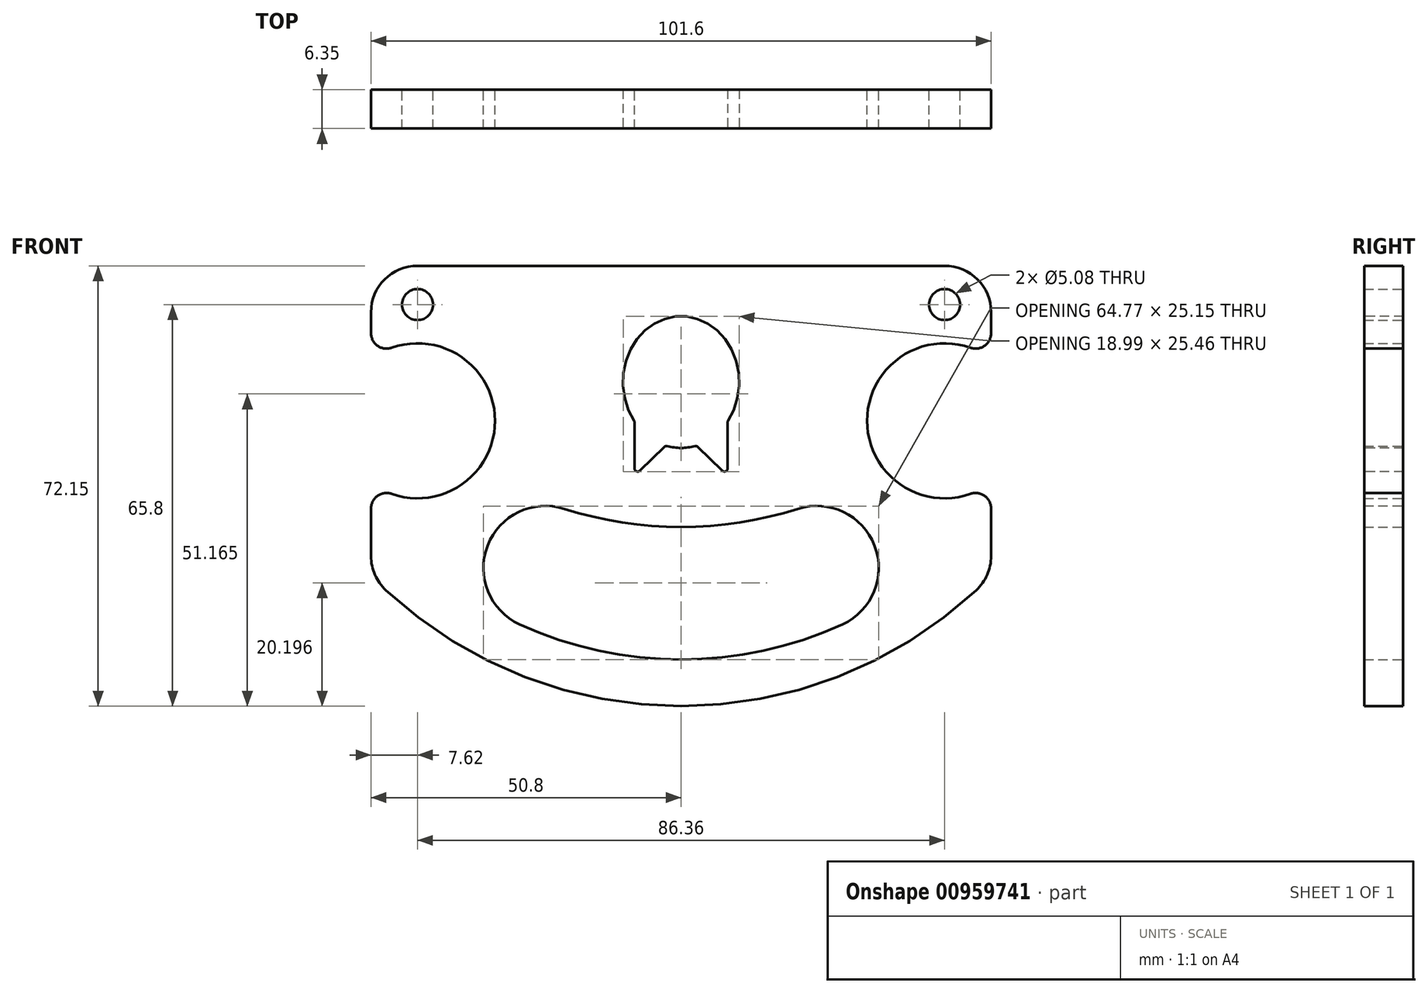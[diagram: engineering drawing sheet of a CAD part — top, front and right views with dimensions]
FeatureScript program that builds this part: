
annotation { "Feature Type Name" : "Feature", "Feature Type Description" : "" }
export const myFeature = defineFeature(function(context is Context, id is Id, definition is map)
    precondition{}
    {
        {
            var Q0;
            Q0=qCreatedBy(makeId("Front.planeOp"),FACE);
            var sketch = newSketch(context, id + "F0", { "sketchPlane" : qUnion([Q0])});
            skLineSegment(sketch, "E0.bottom", {"start": v(-50.8, 25.4) * mm, "end": v(50.8, 25.4) * mm});
            skLineSegment(sketch, "E0.top", {"start": v(-50.8, -25.4) * mm, "end": v(50.8, -25.4) * mm});
            skLineSegment(sketch, "E0.left", {"start": v(-50.8, 25.4) * mm, "end": v(-50.8, 10.16) * mm});
            skLineSegment(sketch, "E0.right", {"start": v(50.8, 25.4) * mm, "end": v(50.8, 10.16) * mm});
            skArc(sketch, "E1", {"start": v(-50.8, -10.16) * mm, "mid": v(-30.48, 0) * mm, "end": v(-50.8, 10.16) * mm});
            skLineSegment(sketch, "E2", {"start": v(0, 25.4) * mm, "end": v(0, -25.4) * mm, "construction": true});
            skArc(sketch, "E3.MirrorCS", {"start": v(50.8, -10.16) * mm, "mid": v(30.48, 0) * mm, "end": v(50.8, 10.16) * mm});
            skLineSegment(sketch, "E4", {"start": v(-43.18, 0) * mm, "end": v(43.18, 0) * mm, "construction": true});
            skPoint(sketch, "E5", {"position": v(0, 0) * mm});
            skLineSegment(sketch, "E6.trimOffspring", {"start": v(-50.8, -10.16) * mm, "end": v(-50.8, -25.4) * mm});
            skLineSegment(sketch, "E7.trimOffspring", {"start": v(50.8, -10.16) * mm, "end": v(50.8, -25.4) * mm});
            skArc(sketch, "E8", {"start": v(-50.8, -25.4) * mm, "mid": v(0, -46.75) * mm, "end": v(50.8, -25.4) * mm});
            skArc(sketch, "E9", {"start": v(-26.46, -33.35) * mm, "mid": v(0, -39.13) * mm, "end": v(26.46, -33.35) * mm});
            skCircle(sketch, "E10", {"center": v(-22.22, -24.12) * mm, "radius": 10.16 * mm});
            skCircle(sketch, "E11.MirrorC", {"center": v(22.22, -24.12) * mm, "radius": 10.16 * mm});
            skArc(sketch, "E12", {"start": v(-19.16, -14.43) * mm, "mid": v(0, -17.39) * mm, "end": v(19.16, -14.43) * mm});
            skCircle(sketch, "E13", {"center": v(-43.18, 19.05) * mm, "radius": 2.54 * mm});
            skCircle(sketch, "E14.MirrorC", {"center": v(43.18, 19.05) * mm, "radius": 2.54 * mm});
            skLineSegment(sketch, "E15", {"start": v(-7.62, -0.13) * mm, "end": v(-7.62, -9.02) * mm});
            skLineSegment(sketch, "E16", {"start": v(-7.62, -9.02) * mm, "end": v(-2.54, -4.05) * mm});
            skEllipse(sketch, "E17", {"center": v(0, 6.35) * mm, "majorRadius": 10.8 * mm, "minorRadius": 9.53 * mm, "majorAxis": v(0, 1)});
            skLineSegment(sketch, "E18", {"start": v(0, 6.35) * mm, "end": v(0, -77.08) * mm, "construction": true});
            skLineSegment(sketch, "E19.MirrorCS", {"start": v(7.62, -0.13) * mm, "end": v(7.62, -9.02) * mm});
            skLineSegment(sketch, "E20.MirrorCS", {"start": v(7.62, -9.02) * mm, "end": v(2.54, -4.05) * mm});
            skSolve(sketch);
        }
        {
            var Q0;
            {var subQ1=sQuery(id+"F0.wireOp",EDGE,"E8");Q0=makeQuery(id+"F0.imprint","IMPRINT",FACE,{"disambiguationData":[TD([[makeQuery(id+"F0.imprint","IMPRINT",EDGE,{"derivedFrom":subQ1}),1.0]])]});}
            var Q1;
            Q1=makeQuery(id+"F0.imprint","IMPRINT",FACE,{"disambiguationData":[TD([[makeQuery(id+"F0.imprint","IMPRINT",EDGE,{"derivedFrom":sQuery(id+"F0.wireOp",EDGE,"E0.bottom")}),-1.0]])]});
            extrude(context, id + "F1", {"entities" : qUnion([Q0, Q1]), "depth" : 6.35 * mm, "offsetDistance" : 25.4 * mm});
        }
        {
            var Q0;
            Q0=makeQuery(id+"F1.opExtrude","SWEPT_EDGE",EDGE,{"disambiguationData":[OSD([sQuery(id+"F0.wireOp",EDGE,"E0.top"),sQuery(id+"F0.wireOp",EDGE,"E7.trimOffspring"),sQuery(id+"F0.wireOp",EDGE,"E8")])]});
            var Q1;
            Q1=makeQuery(id+"F1.opExtrude","SWEPT_EDGE",EDGE,{"disambiguationData":[OSD([sQuery(id+"F0.wireOp",EDGE,"E0.top"),sQuery(id+"F0.wireOp",EDGE,"E6.trimOffspring"),sQuery(id+"F0.wireOp",EDGE,"E8")])]});
            var Q2;
            Q2=makeQuery(id+"F1.opExtrude","SWEPT_EDGE",EDGE,{"disambiguationData":[OSD([sQuery(id+"F0.wireOp",EDGE,"E0.bottom"),sQuery(id+"F0.wireOp",EDGE,"E0.left")])]});
            var Q3;
            Q3=makeQuery(id+"F1.opExtrude","SWEPT_EDGE",EDGE,{"disambiguationData":[OSD([sQuery(id+"F0.wireOp",EDGE,"E0.bottom"),sQuery(id+"F0.wireOp",EDGE,"E0.right")])]});
            fillet(context, id + "F2", {"entities" : qUnion([Q0, Q1, Q2, Q3]), "radius" : 7.62 * mm, "allowEdgeOverflow" : false});
        }
        {
            var Q0;
            Q0=makeQuery(id+"F1.opExtrude","SWEPT_EDGE",EDGE,{"disambiguationData":[OSD([sQuery(id+"F0.wireOp",EDGE,"E1"),sQuery(id+"F0.wireOp",EDGE,"E6.trimOffspring")])]});
            var Q1;
            Q1=makeQuery(id+"F1.opExtrude","SWEPT_EDGE",EDGE,{"disambiguationData":[OSD([sQuery(id+"F0.wireOp",EDGE,"E3.MirrorCS"),sQuery(id+"F0.wireOp",EDGE,"E7.trimOffspring")])]});
            var Q2;
            Q2=makeQuery(id+"F1.opExtrude","SWEPT_EDGE",EDGE,{"disambiguationData":[OSD([sQuery(id+"F0.wireOp",EDGE,"E0.right"),sQuery(id+"F0.wireOp",EDGE,"E3.MirrorCS")])]});
            var Q3;
            Q3=makeQuery(id+"F1.opExtrude","SWEPT_EDGE",EDGE,{"disambiguationData":[OSD([sQuery(id+"F0.wireOp",EDGE,"E0.left"),sQuery(id+"F0.wireOp",EDGE,"E1")])]});
            fillet(context, id + "F3", {"entities" : qUnion([Q0, Q1, Q2, Q3]), "radius" : 2.54 * mm, "tangentPropagation" : true, "allowEdgeOverflow" : false});
        }
        {
            var Q0;
            Q0=makeQuery(id+"F1.opExtrude","SWEPT_EDGE",EDGE,{"disambiguationData":[OSD([sQuery(id+"F0.wireOp",EDGE,"E15"),sQuery(id+"F0.wireOp",EDGE,"E17")])]});
            var Q1;
            Q1=makeQuery(id+"F1.opExtrude","SWEPT_EDGE",EDGE,{"disambiguationData":[OSD([sQuery(id+"F0.wireOp",EDGE,"E16"),sQuery(id+"F0.wireOp",EDGE,"E17")])]});
            var Q2;
            Q2=makeQuery(id+"F1.opExtrude","SWEPT_EDGE",EDGE,{"disambiguationData":[OSD([sQuery(id+"F0.wireOp",EDGE,"E17"),sQuery(id+"F0.wireOp",EDGE,"E20.MirrorCS")])]});
            var Q3;
            Q3=makeQuery(id+"F1.opExtrude","SWEPT_EDGE",EDGE,{"disambiguationData":[OSD([sQuery(id+"F0.wireOp",EDGE,"E15"),sQuery(id+"F0.wireOp",EDGE,"E16")])]});
            var Q4;
            Q4=makeQuery(id+"F1.opExtrude","SWEPT_EDGE",EDGE,{"disambiguationData":[OSD([sQuery(id+"F0.wireOp",EDGE,"E19.MirrorCS"),sQuery(id+"F0.wireOp",EDGE,"E20.MirrorCS")])]});
            var Q5;
            Q5=makeQuery(id+"F1.opExtrude","SWEPT_EDGE",EDGE,{"disambiguationData":[OSD([sQuery(id+"F0.wireOp",EDGE,"E17"),sQuery(id+"F0.wireOp",EDGE,"E19.MirrorCS")])]});
            var Q6;
            Q6=makeQuery(id+"F1.opExtrude","SWEPT_EDGE",EDGE,{"disambiguationData":[OSD([sQuery(id+"F0.wireOp",EDGE,"E15"),sQuery(id+"F0.wireOp",EDGE,"E17")])]});
            var Q7;
            Q7=makeQuery(id+"F1.opExtrude","SWEPT_EDGE",EDGE,{"disambiguationData":[OSD([sQuery(id+"F0.wireOp",EDGE,"E15"),sQuery(id+"F0.wireOp",EDGE,"E16")])]});
            var Q8;
            Q8=makeQuery(id+"F1.opExtrude","SWEPT_EDGE",EDGE,{"disambiguationData":[OSD([sQuery(id+"F0.wireOp",EDGE,"E16"),sQuery(id+"F0.wireOp",EDGE,"E17")])]});
            var Q9;
            Q9=makeQuery(id+"F1.opExtrude","SWEPT_EDGE",EDGE,{"disambiguationData":[OSD([sQuery(id+"F0.wireOp",EDGE,"E17"),sQuery(id+"F0.wireOp",EDGE,"E20.MirrorCS")])]});
            var Q10;
            Q10=makeQuery(id+"F1.opExtrude","SWEPT_EDGE",EDGE,{"disambiguationData":[OSD([sQuery(id+"F0.wireOp",EDGE,"E19.MirrorCS"),sQuery(id+"F0.wireOp",EDGE,"E20.MirrorCS")])]});
            var Q11;
            Q11=makeQuery(id+"F1.opExtrude","SWEPT_EDGE",EDGE,{"disambiguationData":[OSD([sQuery(id+"F0.wireOp",EDGE,"E17"),sQuery(id+"F0.wireOp",EDGE,"E19.MirrorCS")])]});
            var Q12;
            Q12=makeQuery(id+"F1.opExtrude","SWEPT_EDGE",EDGE,{"disambiguationData":[OSD([sQuery(id+"F0.wireOp",EDGE,"E15"),sQuery(id+"F0.wireOp",EDGE,"E16")])]});
            var Q13;
            Q13=makeQuery(id+"F1.opExtrude","SWEPT_EDGE",EDGE,{"disambiguationData":[OSD([sQuery(id+"F0.wireOp",EDGE,"E15"),sQuery(id+"F0.wireOp",EDGE,"E16")])]});
            var Q14;
            Q14=makeQuery(id+"F1.opExtrude","SWEPT_EDGE",EDGE,{"disambiguationData":[OSD([sQuery(id+"F0.wireOp",EDGE,"E15"),sQuery(id+"F0.wireOp",EDGE,"E17")])]});
            var Q15;
            Q15=makeQuery(id+"F1.opExtrude","SWEPT_EDGE",EDGE,{"disambiguationData":[OSD([sQuery(id+"F0.wireOp",EDGE,"E16"),sQuery(id+"F0.wireOp",EDGE,"E17")])]});
            var Q16;
            Q16=makeQuery(id+"F1.opExtrude","SWEPT_EDGE",EDGE,{"disambiguationData":[OSD([sQuery(id+"F0.wireOp",EDGE,"E17"),sQuery(id+"F0.wireOp",EDGE,"E20.MirrorCS")])]});
            var Q17;
            Q17=makeQuery(id+"F1.opExtrude","SWEPT_EDGE",EDGE,{"disambiguationData":[OSD([sQuery(id+"F0.wireOp",EDGE,"E17"),sQuery(id+"F0.wireOp",EDGE,"E19.MirrorCS")])]});
            var Q18;
            Q18=makeQuery(id+"F1.opExtrude","SWEPT_EDGE",EDGE,{"disambiguationData":[OSD([sQuery(id+"F0.wireOp",EDGE,"E15"),sQuery(id+"F0.wireOp",EDGE,"E17")])]});
            fillet(context, id + "F4", {"entities" : qUnion([Q0, Q1, Q2, Q3, Q4, Q5, Q6, Q7, Q8, Q9, Q10, Q11, Q12, Q13, Q14, Q15, Q16, Q17, Q18]), "radius" : 0.5 * mm, "allowEdgeOverflow" : false});
        }
    });
